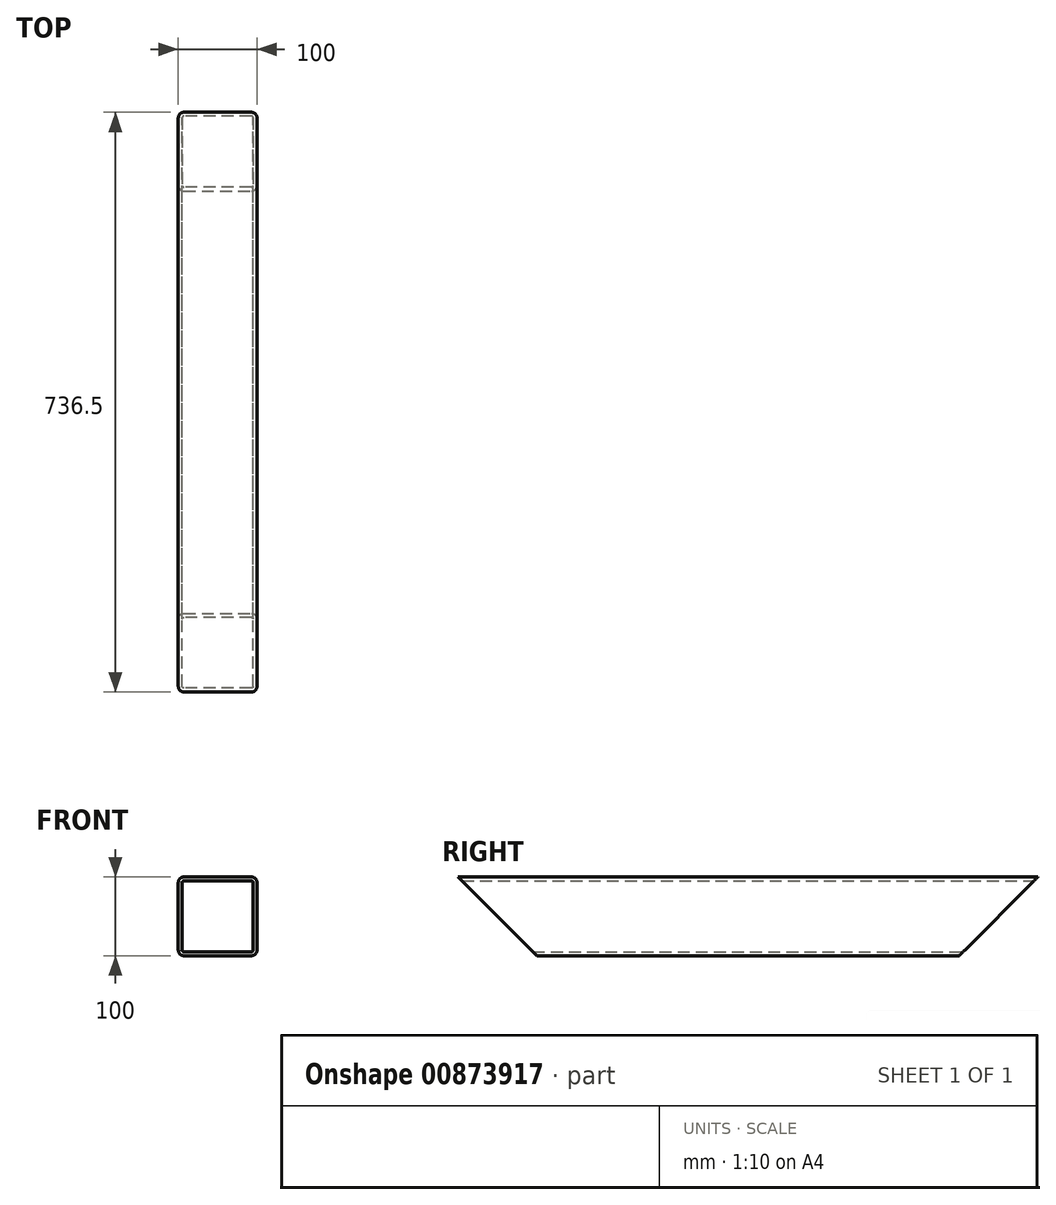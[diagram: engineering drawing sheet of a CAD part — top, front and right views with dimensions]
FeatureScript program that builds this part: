
annotation { "Feature Type Name" : "Feature", "Feature Type Description" : "" }
export const myFeature = defineFeature(function(context is Context, id is Id, definition is map)
    precondition{}
    {
        {
            var Q0;
            Q0=qCreatedBy(makeId("Front.planeOp"),FACE);
            var sketch = newSketch(context, id + "F0", { "sketchPlane" : qUnion([Q0])});
            skLineSegment(sketch, "E0.bottom", {"start": v(43, 50) * mm, "end": v(-43, 50) * mm});
            skLineSegment(sketch, "E0.top", {"start": v(43, -50) * mm, "end": v(-43, -50) * mm});
            skLineSegment(sketch, "E0.left", {"start": v(50, 43) * mm, "end": v(50, -43) * mm});
            skLineSegment(sketch, "E0.right", {"start": v(-50, 43) * mm, "end": v(-50, -43) * mm});
            skPoint(sketch, "E0.middle", {"position": v(0, 0) * mm});
            skPoint(sketch, "E1.visualSharp", {"position": v(-50, 50) * mm});
            skArc(sketch, "E1.filletArc", {"start": v(-43, 50) * mm, "mid": v(-47.95, 47.95) * mm, "end": v(-50, 43) * mm});
            skPoint(sketch, "E2.visualSharp", {"position": v(50, 50) * mm});
            skArc(sketch, "E2.filletArc", {"start": v(50, 43) * mm, "mid": v(47.95, 47.95) * mm, "end": v(43, 50) * mm});
            skPoint(sketch, "E3.visualSharp", {"position": v(-50, -50) * mm});
            skArc(sketch, "E3.filletArc", {"start": v(-50, -43) * mm, "mid": v(-47.95, -47.95) * mm, "end": v(-43, -50) * mm});
            skPoint(sketch, "E4.visualSharp", {"position": v(50, -50) * mm});
            skArc(sketch, "E4.filletArc", {"start": v(43, -50) * mm, "mid": v(47.95, -47.95) * mm, "end": v(50, -43) * mm});
            skLineSegment(sketch, "E5.0", {"start": v(43, -45) * mm, "end": v(-43, -45) * mm});
            skArc(sketch, "E5.1", {"start": v(-45, -43) * mm, "mid": v(-44.41, -44.41) * mm, "end": v(-43, -45) * mm});
            skArc(sketch, "E5.2", {"start": v(43, -45) * mm, "mid": v(44.41, -44.41) * mm, "end": v(45, -43) * mm});
            skLineSegment(sketch, "E5.3", {"start": v(-45, 43) * mm, "end": v(-45, -43) * mm});
            skLineSegment(sketch, "E5.4", {"start": v(45, 43) * mm, "end": v(45, -43) * mm});
            skArc(sketch, "E5.5", {"start": v(45, 43) * mm, "mid": v(44.41, 44.41) * mm, "end": v(43, 45) * mm});
            skLineSegment(sketch, "E5.6", {"start": v(43, 45) * mm, "end": v(-43, 45) * mm});
            skArc(sketch, "E5.7", {"start": v(-43, 45) * mm, "mid": v(-44.41, 44.41) * mm, "end": v(-45, 43) * mm});
            skSolve(sketch);
        }
        {
            var Q0;
            Q0=makeQuery(id+"F0.imprint","IMPRINT",FACE,{"disambiguationData":[TD([[makeQuery(id+"F0.imprint","IMPRINT",EDGE,{"derivedFrom":sQuery(id+"F0.wireOp",EDGE,"E0.bottom")}),1.0]])]});
            extrude(context, id + "F1", {"entities" : qUnion([Q0]), "depth" : 736.5 * mm, "offsetDistance" : 25 * mm, "symmetric" : true});
        }
        {
            var Q0;
            Q0=makeQuery(id+"F1.opExtrude","SWEPT_FACE",FACE,{"disambiguationData":[OSD([sQuery(id+"F0.wireOp",EDGE,"E0.left")])]});
            var sketch = newSketch(context, id + "F2", { "sketchPlane" : qUnion([Q0])});
            skLineSegment(sketch, "E6.top", {"start": v(-268.25, -50) * mm, "end": v(-368.25, -50) * mm});
            skPoint(sketch, "E6.middle", {"position": v(-368.25, 0) * mm});
            skLineSegment(sketch, "E7", {"start": v(-368.25, 50) * mm, "end": v(-268.25, -50) * mm});
            skLineSegment(sketch, "E8", {"start": v(-368.25, 50) * mm, "end": v(-368.25, -50) * mm});
            skLineSegment(sketch, "E9.MirrorCS", {"start": v(268.25, -50) * mm, "end": v(368.25, -50) * mm});
            skLineSegment(sketch, "E10.MirrorCS", {"start": v(368.25, 50) * mm, "end": v(368.25, -50) * mm});
            skPoint(sketch, "E11.MirrorP", {"position": v(368.25, 0) * mm});
            skLineSegment(sketch, "E12.MirrorCS", {"start": v(368.25, 50) * mm, "end": v(268.25, -50) * mm});
            skSolve(sketch);
        }
        {
            var Q0;
            Q0 = qSketchRegion(id + "F2", true);
            extrude(context, id + "F3", {"entities" : qUnion([Q0]), "operationType" : NewBodyOperationType.REMOVE, "endBound" : BoundingType.THROUGH_ALL, "oppositeDirection" : true, "depth" : 25 * mm, "offsetDistance" : 25 * mm});
        }
    });
